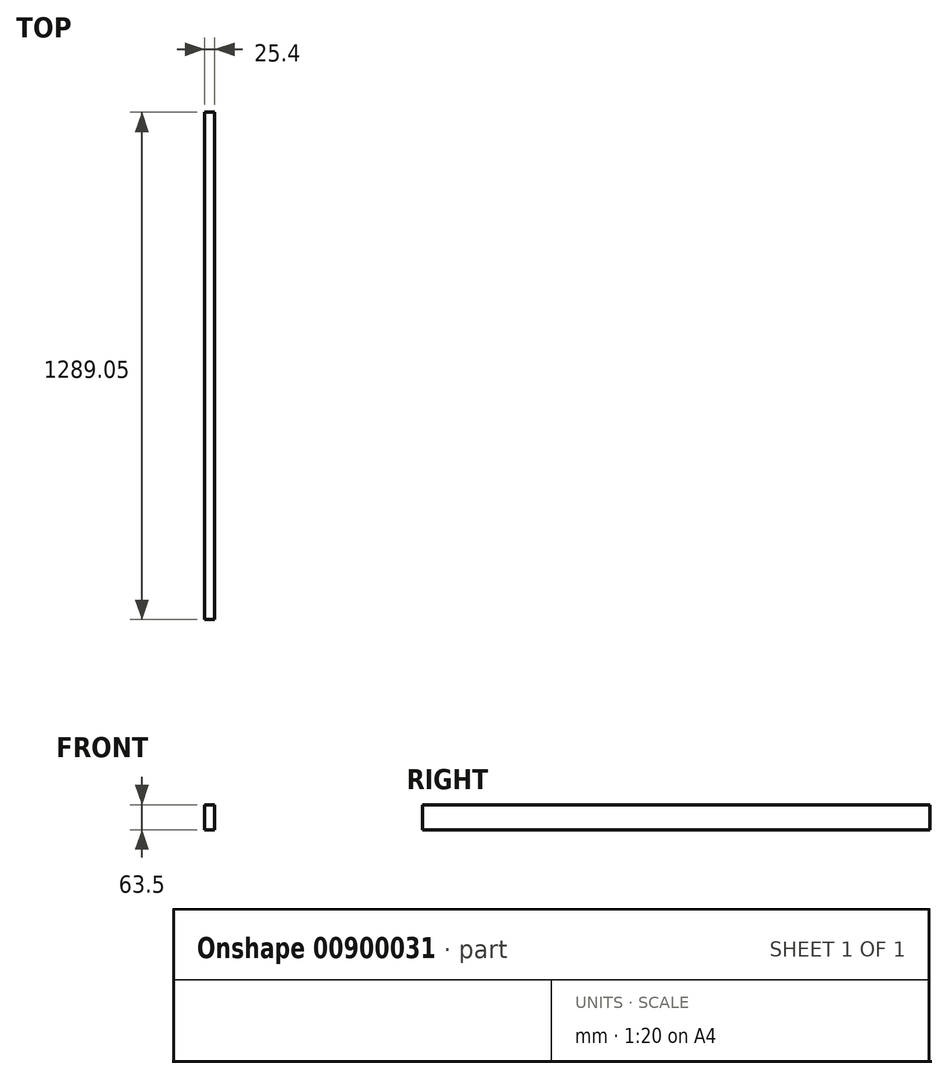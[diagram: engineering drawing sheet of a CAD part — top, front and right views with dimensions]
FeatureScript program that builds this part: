
annotation { "Feature Type Name" : "Feature", "Feature Type Description" : "" }
export const myFeature = defineFeature(function(context is Context, id is Id, definition is map)
    precondition{}
    {
        {
            var Q0;
            Q0=qCreatedBy(makeId("Top.planeOp"),FACE);
            var sketch = newSketch(context, id + "F0", { "sketchPlane" : qUnion([Q0])});
            skLineSegment(sketch, "E0.bottom", {"start": v(0, 0) * mm, "end": v(25.4, 0) * mm});
            skLineSegment(sketch, "E0.top", {"start": v(0, 1289.05) * mm, "end": v(25.4, 1289.05) * mm});
            skLineSegment(sketch, "E0.left", {"start": v(0, 0) * mm, "end": v(0, 1289.05) * mm});
            skLineSegment(sketch, "E0.right", {"start": v(25.4, 0) * mm, "end": v(25.4, 1289.05) * mm});
            skSolve(sketch);
        }
        {
            var Q0;
            Q0 = qSketchRegion(id + "F0", true);
            extrude(context, id + "F1", {"entities" : qUnion([Q0]), "depth" : 63.5 * mm, "offsetDistance" : 25.4 * mm});
        }
    });
